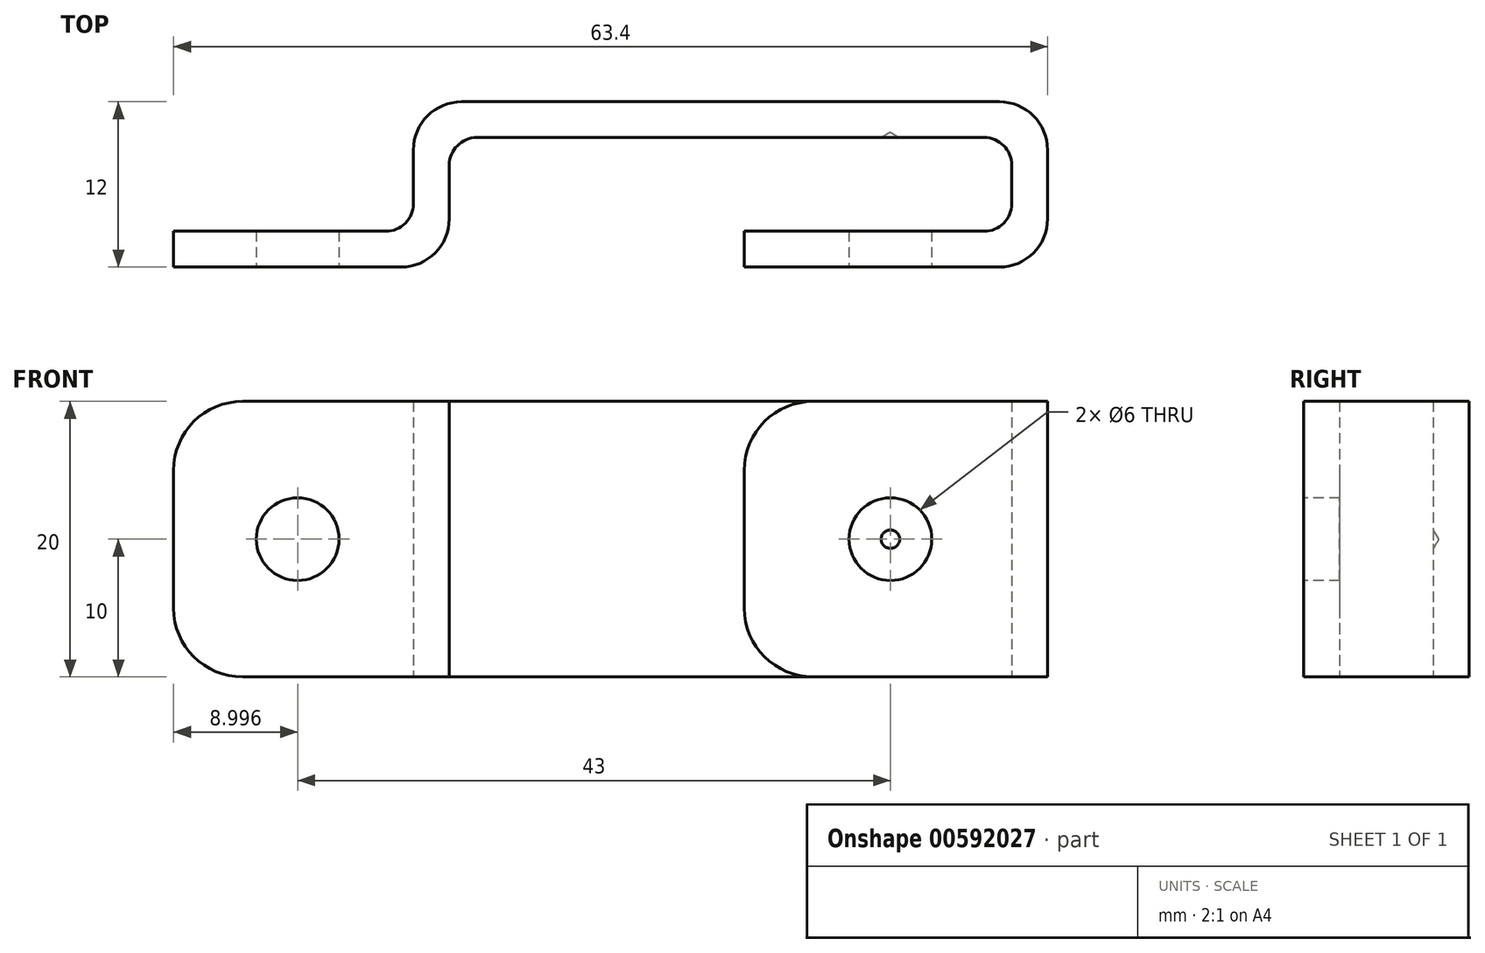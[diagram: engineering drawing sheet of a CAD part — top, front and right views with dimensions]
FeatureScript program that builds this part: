
annotation { "Feature Type Name" : "Feature", "Feature Type Description" : "" }
export const myFeature = defineFeature(function(context is Context, id is Id, definition is map)
    precondition{}
    {
        {
            var Q0;
            Q0=qCreatedBy(makeId("Top.planeOp"),FACE);
            var sketch = newSketch(context, id + "F0", { "sketchPlane" : qUnion([Q0])});
            skLineSegment(sketch, "E0", {"start": v(-46.56, 0) * mm, "end": v(-26.56, 0) * mm});
            skLineSegment(sketch, "E1", {"start": v(-26.56, 0) * mm, "end": v(-26.56, 9.4) * mm});
            skLineSegment(sketch, "E2", {"start": v(-26.56, 9.4) * mm, "end": v(14.24, 9.4) * mm});
            skLineSegment(sketch, "E3", {"start": v(14.24, 9.4) * mm, "end": v(14.24, 2.6) * mm});
            skLineSegment(sketch, "E4", {"start": v(14.24, 2.6) * mm, "end": v(-5.16, 2.6) * mm});
            skLineSegment(sketch, "E5", {"start": v(-5.16, 2.6) * mm, "end": v(-5.16, 0) * mm});
            skLineSegment(sketch, "E6", {"start": v(-5.16, 0) * mm, "end": v(16.84, 0) * mm});
            skLineSegment(sketch, "E7", {"start": v(16.84, 0) * mm, "end": v(16.84, 12) * mm});
            skLineSegment(sketch, "E8", {"start": v(16.84, 12) * mm, "end": v(-29.16, 12) * mm});
            skLineSegment(sketch, "E9", {"start": v(-29.16, 12) * mm, "end": v(-29.16, 2.6) * mm});
            skLineSegment(sketch, "E10", {"start": v(-29.16, 2.6) * mm, "end": v(-46.56, 2.6) * mm});
            skLineSegment(sketch, "E11", {"start": v(-46.56, 2.6) * mm, "end": v(-46.56, 0) * mm});
            skSolve(sketch);
        }
        {
            var Q0;
            Q0=makeQuery(id+"F0.imprint","IMPRINT",FACE,{"disambiguationData":[TD([[makeQuery(id+"F0.imprint","IMPRINT",EDGE,{"derivedFrom":sQuery(id+"F0.wireOp",EDGE,"E0")}),1.0]])]});
            extrude(context, id + "F1", {"entities" : qUnion([Q0]), "depth" : 20 * mm, "offsetDistance" : 25 * mm});
        }
        {
            var Q0;
            Q0=makeQuery(id+"F1.opExtrude","SWEPT_EDGE",EDGE,{"disambiguationData":[OSD([sQuery(id+"F0.wireOp",EDGE,"E9"),sQuery(id+"F0.wireOp",EDGE,"E10")])]});
            var Q1;
            Q1=makeQuery(id+"F1.opExtrude","SWEPT_EDGE",EDGE,{"disambiguationData":[OSD([sQuery(id+"F0.wireOp",EDGE,"E3"),sQuery(id+"F0.wireOp",EDGE,"E4")])]});
            var Q2;
            Q2=makeQuery(id+"F1.opExtrude","SWEPT_EDGE",EDGE,{"disambiguationData":[OSD([sQuery(id+"F0.wireOp",EDGE,"E2"),sQuery(id+"F0.wireOp",EDGE,"E3")])]});
            var Q3;
            Q3=makeQuery(id+"F1.opExtrude","SWEPT_EDGE",EDGE,{"disambiguationData":[OSD([sQuery(id+"F0.wireOp",EDGE,"E1"),sQuery(id+"F0.wireOp",EDGE,"E2")])]});
            fillet(context, id + "F2", {"entities" : qUnion([Q0, Q1, Q2, Q3]), "tangentPropagation" : true, "radius" : 2 * mm, "defaultsChanged" : false, "vertexSettings" : [], "allowEdgeOverflow" : false});
        }
        {
            var Q0;
            Q0=makeQuery(id+"F1.opExtrude","SWEPT_EDGE",EDGE,{"disambiguationData":[OSD([sQuery(id+"F0.wireOp",EDGE,"E7"),sQuery(id+"F0.wireOp",EDGE,"E8")])]});
            var Q1;
            Q1=makeQuery(id+"F1.opExtrude","SWEPT_EDGE",EDGE,{"disambiguationData":[OSD([sQuery(id+"F0.wireOp",EDGE,"E8"),sQuery(id+"F0.wireOp",EDGE,"E9")])]});
            var Q2;
            Q2=makeQuery(id+"F1.opExtrude","SWEPT_EDGE",EDGE,{"disambiguationData":[OSD([sQuery(id+"F0.wireOp",EDGE,"E0"),sQuery(id+"F0.wireOp",EDGE,"E1")])]});
            var Q3;
            Q3=makeQuery(id+"F1.opExtrude","SWEPT_EDGE",EDGE,{"disambiguationData":[OSD([sQuery(id+"F0.wireOp",EDGE,"E6"),sQuery(id+"F0.wireOp",EDGE,"E7")])]});
            fillet(context, id + "F3", {"entities" : qUnion([Q0, Q1, Q2, Q3]), "tangentPropagation" : true, "radius" : 3.5 * mm, "defaultsChanged" : false, "vertexSettings" : [], "allowEdgeOverflow" : false});
        }
        {
            var Q0;
            Q0=makeQuery(id+"F1.opExtrude","CAP_EDGE",EDGE,{"disambiguationData":[OSD([sQuery(id+"F0.wireOp",EDGE,"E11")])],"isStart":true});
            var Q1;
            Q1=makeQuery(id+"F1.opExtrude","CAP_EDGE",EDGE,{"disambiguationData":[OSD([sQuery(id+"F0.wireOp",EDGE,"E11")])],"isStart":false});
            var Q2;
            Q2=makeQuery(id+"F1.opExtrude","CAP_EDGE",EDGE,{"disambiguationData":[OSD([sQuery(id+"F0.wireOp",EDGE,"E5")])],"isStart":false});
            var Q3;
            Q3=makeQuery(id+"F1.opExtrude","CAP_EDGE",EDGE,{"disambiguationData":[OSD([sQuery(id+"F0.wireOp",EDGE,"E5")])],"isStart":true});
            fillet(context, id + "F4", {"entities" : qUnion([Q0, Q1, Q2, Q3]), "tangentPropagation" : true, "radius" : 5 * mm, "defaultsChanged" : false, "vertexSettings" : [], "allowEdgeOverflow" : false});
        }
        {
            var Q0;
            Q0=makeQuery(id+"F1.opExtrude","SWEPT_FACE",FACE,{"disambiguationData":[OSD([sQuery(id+"F0.wireOp",EDGE,"E0")])]});
            var sketch = newSketch(context, id + "F5", { "sketchPlane" : qUnion([Q0])});
            skPoint(sketch, "E12", {"position": v(-37.56, 10) * mm});
            skPoint(sketch, "E12.positionSnap0", {"position": v(-46.56, 10) * mm});
            skPoint(sketch, "E13", {"position": v(5.44, 10) * mm});
            skSolve(sketch);
        }
        {
            var Q0;
            Q0=sQuery(id+"F5.wireOp",VERTEX,"E12");
            var Q1;
            Q1=sQuery(id+"F5.wireOp",VERTEX,"E13");
            var Q2;
            Q2=makeQuery(id+"F1.opExtrude","SWEPT_BODY",BODY,{"disambiguationData":[OSD([sQuery(id+"F0.wireOp",EDGE,"E0"),sQuery(id+"F0.wireOp",EDGE,"E1"),sQuery(id+"F0.wireOp",EDGE,"E2"),sQuery(id+"F0.wireOp",EDGE,"E3"),sQuery(id+"F0.wireOp",EDGE,"E4"),sQuery(id+"F0.wireOp",EDGE,"E5"),sQuery(id+"F0.wireOp",EDGE,"E6"),sQuery(id+"F0.wireOp",EDGE,"E7"),sQuery(id+"F0.wireOp",EDGE,"E8"),sQuery(id+"F0.wireOp",EDGE,"E9"),sQuery(id+"F0.wireOp",EDGE,"E10"),sQuery(id+"F0.wireOp",EDGE,"E11")])]});
            hole(context, id + "F6", {"style" : HoleStyle.SIMPLE, "endStyle" : HoleEndStyle.BLIND, "holeDiameter" : 6 * mm, "majorDiameter" : 5 * mm, "holeDepth" : 8 * mm, "isTappedThrough" : true, "tappedDepth" : 12 * mm, "tapClearance" : 3, "locations" : qUnion([Q0, Q1]), "scope" : qUnion([Q2])});
        }
    });
